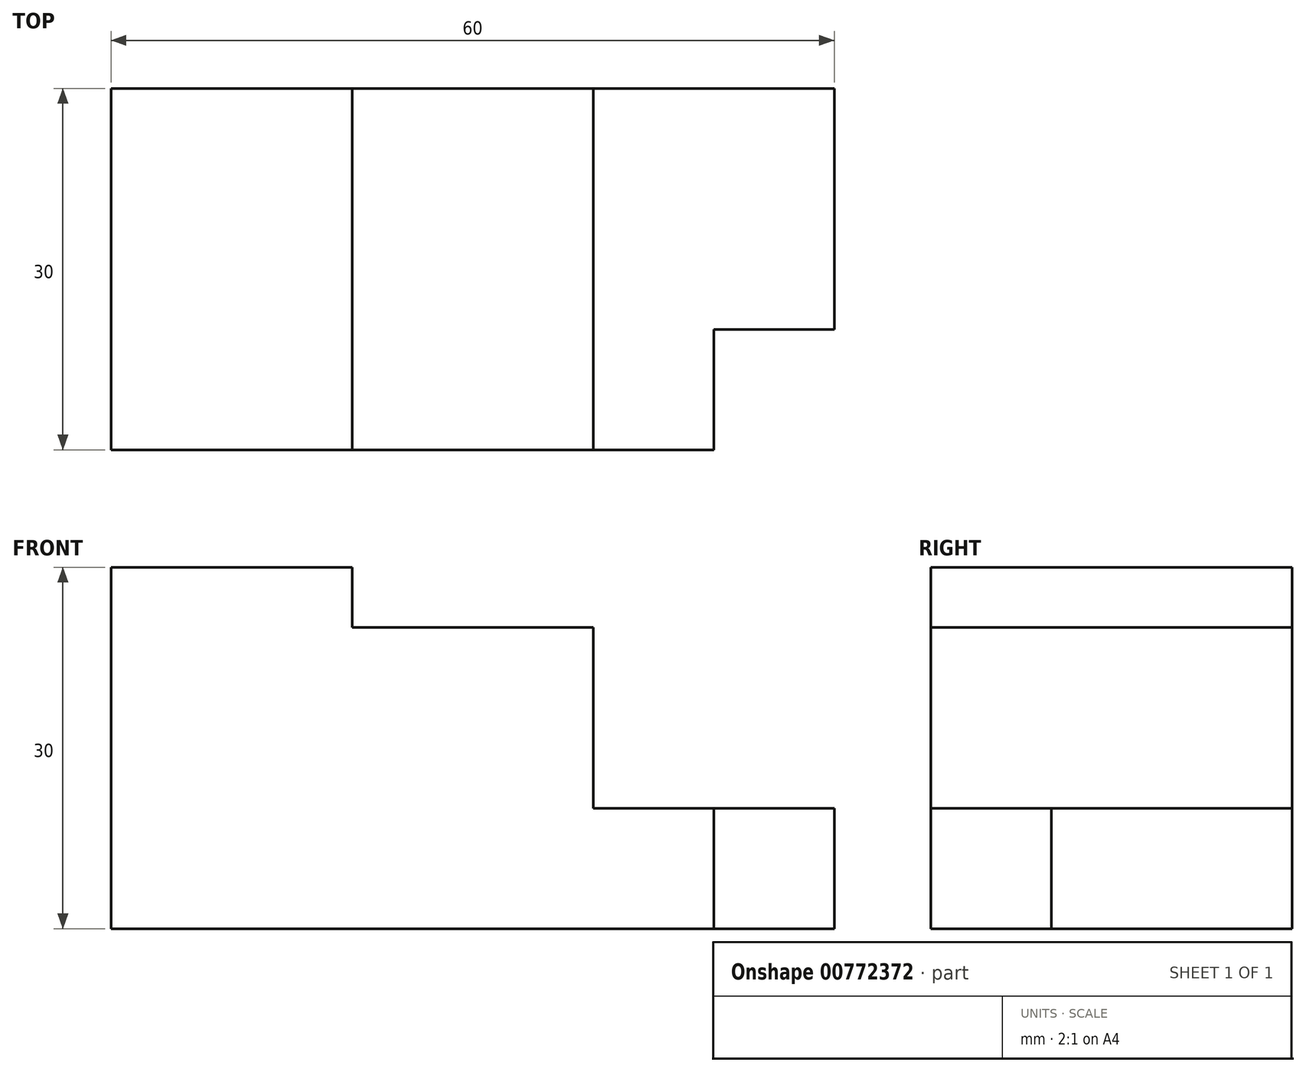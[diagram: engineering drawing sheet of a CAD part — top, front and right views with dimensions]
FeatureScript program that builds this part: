
annotation { "Feature Type Name" : "Feature", "Feature Type Description" : "" }
export const myFeature = defineFeature(function(context is Context, id is Id, definition is map)
    precondition{}
    {
        {
            var Q0;
            Q0=qCreatedBy(makeId("Front.planeOp"),FACE);
            var sketch = newSketch(context, id + "F0", { "sketchPlane" : qUnion([Q0])});
            skLineSegment(sketch, "E0", {"start": v(0, 0) * mm, "end": v(0, 30) * mm});
            skLineSegment(sketch, "E1", {"start": v(0, 30) * mm, "end": v(20, 30) * mm});
            skLineSegment(sketch, "E2", {"start": v(20, 30) * mm, "end": v(20, 25) * mm});
            skLineSegment(sketch, "E3", {"start": v(20, 25) * mm, "end": v(40, 25) * mm});
            skLineSegment(sketch, "E4", {"start": v(40, 25) * mm, "end": v(40, 10) * mm});
            skLineSegment(sketch, "E5", {"start": v(40, 10) * mm, "end": v(60, 10) * mm});
            skLineSegment(sketch, "E6", {"start": v(60, 10) * mm, "end": v(60, 0) * mm});
            skLineSegment(sketch, "E7", {"start": v(60, 0) * mm, "end": v(0, 0) * mm});
            skLineSegment(sketch, "E8", {"start": v(50, 0) * mm, "end": v(50, 10) * mm});
            skSolve(sketch);
        }
        {
            var Q0;
            {var subQ0=sQuery(id+"F0.wireOp",EDGE,"E0");Q0=makeQuery(id+"F0.imprint","IMPRINT",FACE,{"disambiguationData":[TD([[makeQuery(id+"F0.imprint","IMPRINT",EDGE,{"derivedFrom":subQ0}),-1.0]])]});}
            var Q1;
            {var subQ0=sQuery(id+"F0.wireOp",EDGE,"E6");Q1=makeQuery(id+"F0.imprint","IMPRINT",FACE,{"disambiguationData":[TD([[makeQuery(id+"F0.imprint","IMPRINT",EDGE,{"derivedFrom":subQ0}),-1.0]])]});}
            extrude(context, id + "F1", {"entities" : qUnion([Q0, Q1]), "depth" : 20 * mm, "offsetDistance" : 25 * mm});
        }
        {
            var Q0;
            {var subQ0=sQuery(id+"F0.wireOp",EDGE,"E0");Q0=makeQuery(id+"F0.imprint","IMPRINT",FACE,{"disambiguationData":[TD([[makeQuery(id+"F0.imprint","IMPRINT",EDGE,{"derivedFrom":subQ0}),-1.0]])]});}
            extrude(context, id + "F2", {"entities" : qUnion([Q0]), "operationType" : NewBodyOperationType.ADD, "depth" : 30 * mm, "offsetDistance" : 25 * mm});
        }
    });
